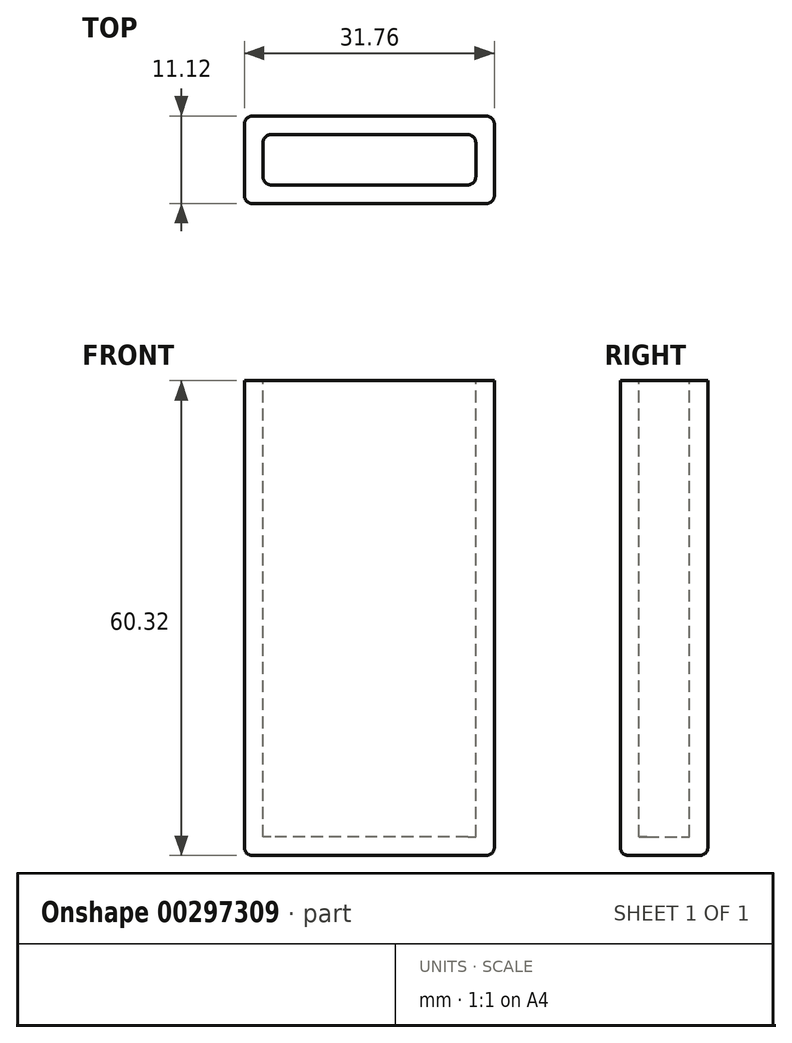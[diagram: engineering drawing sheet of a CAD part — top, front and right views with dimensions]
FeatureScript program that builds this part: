
annotation { "Feature Type Name" : "Feature", "Feature Type Description" : "" }
export const myFeature = defineFeature(function(context is Context, id is Id, definition is map)
    precondition{}
    {
        {
            var Q0;
            Q0=qCreatedBy(makeId("Top.planeOp"),FACE);
            var sketch = newSketch(context, id + "F0", { "sketchPlane" : qUnion([Q0])});
            skLineSegment(sketch, "E0.bottom", {"start": v(15.88, -5.56) * mm, "end": v(-15.88, -5.56) * mm});
            skLineSegment(sketch, "E0.top", {"start": v(15.88, 5.56) * mm, "end": v(-15.88, 5.56) * mm});
            skLineSegment(sketch, "E0.left", {"start": v(15.88, -5.56) * mm, "end": v(15.88, 5.56) * mm});
            skLineSegment(sketch, "E0.right", {"start": v(-15.88, -5.56) * mm, "end": v(-15.88, 5.56) * mm});
            skPoint(sketch, "E0.middle", {"position": v(0, 0) * mm});
            skSolve(sketch);
        }
        {
            var Q0;
            Q0=qSketchRegion(id+"F0",true);
            extrude(context, id + "F1", {"entities" : qUnion([Q0]), "depth" : 60.32 * mm});
        }
        {
            var Q0;
            Q0=makeQuery(id+"F1.opExtrude","CAP_FACE",FACE,{"disambiguationData":[OSD([sQuery(id+"F0.wireOp",EDGE,"E0.bottom"),sQuery(id+"F0.wireOp",EDGE,"E0.top"),sQuery(id+"F0.wireOp",EDGE,"E0.left"),sQuery(id+"F0.wireOp",EDGE,"E0.right")])],"isStart":false});
            var sketch = newSketch(context, id + "F2", { "sketchPlane" : qUnion([Q0])});
            skLineSegment(sketch, "E1.bottom", {"start": v(13.51, -3.2) * mm, "end": v(-13.51, -3.2) * mm});
            skLineSegment(sketch, "E1.top", {"start": v(13.51, 3.2) * mm, "end": v(-13.51, 3.2) * mm});
            skLineSegment(sketch, "E1.left", {"start": v(13.51, -3.2) * mm, "end": v(13.51, 3.2) * mm});
            skLineSegment(sketch, "E1.right", {"start": v(-13.51, -3.2) * mm, "end": v(-13.51, 3.2) * mm});
            skPoint(sketch, "E1.middle", {"position": v(0, 0) * mm});
            skSolve(sketch);
        }
        {
            var Q0;
            Q0=qSketchRegion(id+"F2",true);
            extrude(context, id + "F3", {"entities" : qUnion([Q0]), "operationType" : NewBodyOperationType.REMOVE, "oppositeDirection" : true, "depth" : 57.96 * mm});
        }
        {
            var Q0;
            Q0=makeQuery(id+"F1.opExtrude","SWEPT_EDGE",EDGE,{"disambiguationData":[OSD([sQuery(id+"F0.wireOp",EDGE,"E0.bottom"),sQuery(id+"F0.wireOp",EDGE,"E0.right")])]});
            var Q1;
            Q1=makeQuery(id+"F1.opExtrude","SWEPT_EDGE",EDGE,{"disambiguationData":[OSD([sQuery(id+"F0.wireOp",EDGE,"E0.bottom"),sQuery(id+"F0.wireOp",EDGE,"E0.left")])]});
            var Q2;
            Q2=makeQuery(id+"F1.opExtrude","SWEPT_EDGE",EDGE,{"disambiguationData":[OSD([sQuery(id+"F0.wireOp",EDGE,"E0.top"),sQuery(id+"F0.wireOp",EDGE,"E0.left")])]});
            var Q3;
            Q3=makeQuery(id+"F1.opExtrude","SWEPT_EDGE",EDGE,{"disambiguationData":[OSD([sQuery(id+"F0.wireOp",EDGE,"E0.top"),sQuery(id+"F0.wireOp",EDGE,"E0.right")])]});
            var Q4;
            Q4=makeQuery(id+"F3.boolean.opBoolean","COPY",EDGE,{"derivedFrom":makeQuery(id+"F3.opExtrude","SWEPT_EDGE",EDGE,{"disambiguationData":[OSD([sQuery(id+"F2.wireOp",EDGE,"E1.top"),sQuery(id+"F2.wireOp",EDGE,"E1.left")])]})});
            var Q5;
            Q5=makeQuery(id+"F3.boolean.opBoolean","COPY",EDGE,{"derivedFrom":makeQuery(id+"F3.opExtrude","SWEPT_EDGE",EDGE,{"disambiguationData":[OSD([sQuery(id+"F2.wireOp",EDGE,"E1.top"),sQuery(id+"F2.wireOp",EDGE,"E1.right")])]})});
            var Q6;
            Q6=makeQuery(id+"F3.boolean.opBoolean","COPY",EDGE,{"derivedFrom":makeQuery(id+"F3.opExtrude","SWEPT_EDGE",EDGE,{"disambiguationData":[OSD([sQuery(id+"F2.wireOp",EDGE,"E1.bottom"),sQuery(id+"F2.wireOp",EDGE,"E1.right")])]})});
            var Q7;
            Q7=makeQuery(id+"F3.boolean.opBoolean","COPY",EDGE,{"derivedFrom":makeQuery(id+"F3.opExtrude","SWEPT_EDGE",EDGE,{"disambiguationData":[OSD([sQuery(id+"F2.wireOp",EDGE,"E1.bottom"),sQuery(id+"F2.wireOp",EDGE,"E1.left")])]})});
            var Q8;
            Q8=makeQuery(id+"F1.opExtrude","CAP_FACE",FACE,{"disambiguationData":[OSD([sQuery(id+"F0.wireOp",EDGE,"E0.bottom"),sQuery(id+"F0.wireOp",EDGE,"E0.top"),sQuery(id+"F0.wireOp",EDGE,"E0.left"),sQuery(id+"F0.wireOp",EDGE,"E0.right")])],"isStart":true});
            fillet(context, id + "F4", {"entities" : qUnion([Q0, Q1, Q2, Q3, Q4, Q5, Q6, Q7, Q8]), "radius" : 1.02 * mm, "tangentPropagation" : true, "allowEdgeOverflow" : false});
        }
    });
